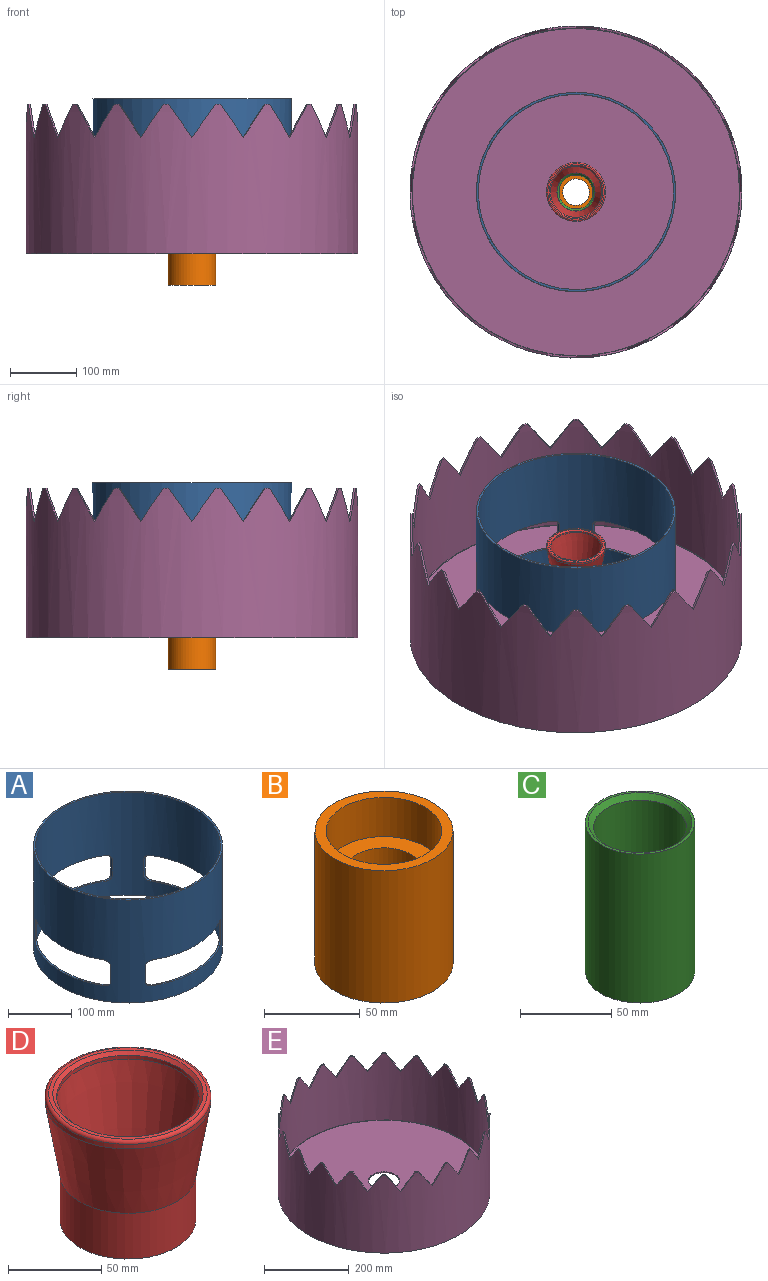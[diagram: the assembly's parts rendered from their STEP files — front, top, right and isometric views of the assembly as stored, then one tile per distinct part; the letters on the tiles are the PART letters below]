
ASSEMBLY  parts=5 mates=4
PART A: 36 faces, bbox 300x300x200 mm
  f0: plane 150x23.57mm, normal (0,0,-1), area 471.7mm2, adj f9,f15,f16,f17
  f1: cylinder r=10mm len=10mm, axis (1,0,0), area 56.4mm2, adj f2,f8,f16,f17
  f2: plane 30x3.66mm, normal (0,1,0), area 109.8mm2, adj f1,f3,f16,f17
  f3: cylinder r=10mm len=10mm, axis (1,0,0), area 56.4mm2, adj f2,f12,f16,f17
  f4: plane 150x23.57mm, normal (0,0,1), area 471.7mm2, adj f11,f13,f16,f17
  f5: cylinder r=10mm len=10mm, axis (1,0,0), area 56.4mm2, adj f6,f12,f16,f17
  f6: plane 30x3.66mm, normal (0,-1,0), area 109.8mm2, adj f5,f7,f16,f17
  f7: cylinder r=10mm len=10mm, axis (1,0,0), area 56.4mm2, adj f6,f8,f16,f17
  f8: plane 150x23.57mm, normal (0,0,-1), area 471.7mm2, adj f1,f7,f16,f17
  f9: cylinder r=10mm len=10mm, axis (1,0,0), area 56.4mm2, adj f0,f10,f16,f17
  f10: plane 30x3.66mm, normal (0,1,0), area 109.8mm2, adj f9,f11,f16,f17
  f11: cylinder r=10mm len=10mm, axis (1,0,0), area 56.4mm2, adj f4,f10,f16,f17
  f12: plane 150x23.57mm, normal (0,0,1), area 471.7mm2, adj f3,f5,f16,f17
  f13: cylinder r=10mm len=10mm, axis (1,0,0), area 56.4mm2, adj f4,f14,f16,f17
  f14: plane 30x3.66mm, normal (0,-1,0), area 109.8mm2, adj f13,f15,f16,f17
  f15: cylinder r=10mm len=10mm, axis (1,0,0), area 56.4mm2, adj f0,f14,f16,f17
  f16: cylinder r=147mm len=294mm, axis (0,0,-1), area 148887.5mm2, adj f0,f1,f2,f3,f4,f5,f6,f7
  f17: cylinder r=150mm len=300mm, axis (0,0,-1), area 152760mm2, adj f0,f1,f2,f3,f4,f5,f6,f7
  f18: plane 300x300mm, normal (0,0,1), area 2799.2mm2, adj f16,f17
  f19: plane 300x300mm, normal (0,0,-1), area 2799.2mm2, adj f16,f17
  f20: cylinder r=10mm len=10mm, axis (0,-1,0), area 56.4mm2, adj f16,f17,f21,f27
  f21: plane 30x3.66mm, normal (-1,0,0), area 109.8mm2, adj f16,f17,f20,f22
  f22: cylinder r=10mm len=10mm, axis (0,-1,0), area 56.4mm2, adj f16,f17,f21,f23
  f23: plane 150x23.57mm, normal (0,0,1), area 471.7mm2, adj f16,f17,f22,f24
  f24: cylinder r=10mm len=10mm, axis (0,-1,0), area 56.4mm2, adj f16,f17,f23,f25
  f25: plane 30x3.66mm, normal (1,0,0), area 109.8mm2, adj f16,f17,f24,f26
  f26: cylinder r=10mm len=10mm, axis (0,-1,0), area 56.4mm2, adj f16,f17,f25,f27
  f27: plane 150x23.57mm, normal (0,0,-1), area 471.7mm2, adj f16,f17,f20,f26
  f28: plane 150x23.57mm, normal (0,0,-1), area 471.7mm2, adj f16,f17,f29,f35
  f29: cylinder r=10mm len=10mm, axis (0,-1,0), area 56.4mm2, adj f16,f17,f28,f30
  f30: plane 30x3.66mm, normal (1,0,0), area 109.8mm2, adj f16,f17,f29,f31
  f31: cylinder r=10mm len=10mm, axis (0,-1,0), area 56.4mm2, adj f16,f17,f30,f32
  f32: plane 150x23.57mm, normal (0,0,1), area 471.7mm2, adj f16,f17,f31,f33
  f33: cylinder r=10mm len=10mm, axis (0,-1,0), area 56.4mm2, adj f16,f17,f32,f34
  f34: plane 30x3.66mm, normal (-1,0,0), area 109.8mm2, adj f16,f17,f33,f35
  f35: cylinder r=10mm len=10mm, axis (0,-1,0), area 56.4mm2, adj f16,f17,f28,f34
PART B: 8 faces, bbox 72x72x84.5 mm
  f0: cylinder r=24.2mm len=48.4mm, axis (0,0,-1), area 3801.3mm2, adj f1,f7
  f1: plane 72x72mm, normal (0,0,-1), area 2231.7mm2, adj f0,f2
  f2: cylinder r=36mm len=84.5mm, axis (0,0,-1), area 19113.4mm2, adj f1,f3
  f3: plane 72x72mm, normal (0,0,1), area 1206.2mm2, adj f2,f4
  f4: cylinder r=30.2mm len=60.4mm, axis (0,0,-1), area 4743.8mm2, adj f3,f5
  f5: plane 60.4x60.4mm, normal (0,0,1), area 1608.6mm2, adj f4,f6
  f6: cylinder r=20mm len=40mm, axis (0,0,-1), area 4335.4mm2, adj f5,f7
  f7: plane 48.4x48.4mm, normal (0,0,-1), area 583.2mm2, adj f0,f6
PART C: 6 faces, bbox 60x60x100 mm
  f0: cylinder r=25.5mm len=94mm, axis (0,0,-1), area 15060.8mm2, adj f4,f5
  f1: cylinder r=30mm len=100mm, axis (0,0,-1), area 18849.6mm2, adj f2,f3
  f2: plane 60x60mm, normal (0,0,1), area 275.7mm2, adj f1,f4
  f3: plane 60x60mm, normal (0,0,-1), area 275.7mm2, adj f1,f5
  f4: cone r=25.5mm half-angle=45deg, axis (0,0,1), area 719.7mm2, adj f0,f2
  f5: cone r=28.5mm half-angle=45deg, axis (0,0,-1), area 719.7mm2, adj f0,f3
PART D: 11 faces, bbox 96.3x96.3x83 mm
  f0: plane 85x85mm, normal (0,0,1), area 572.3mm2, adj f9,f10
  f1: cylinder r=38.3mm len=76.6mm, axis (0,0,-1), area 596.9mm2, adj f2,f10
  f2: cone r=29.27mm half-angle=9.6deg, axis (0,0,1), area 11521.4mm2, adj f1,f3
  f3: plane 60.4x60.4mm, normal (0,0,-1), area 174mm2, adj f2,f4
  f4: cylinder r=30.2mm len=60.4mm, axis (0,0,-1), area 4743.8mm2, adj f3,f5
  f5: plane 72.8x72.8mm, normal (0,0,-1), area 1297.2mm2, adj f4,f6
  f6: cylinder r=36.4mm len=72.8mm, axis (0,0,-1), area 6861.2mm2, adj f5,f7
  f7: cone r=36.4mm half-angle=9.6deg, axis (0,0,1), area 12371.9mm2, adj f6,f8
  f8: cylinder r=44.5mm len=89mm, axis (0,0,-1), area 838.8mm2, adj f7,f9
  f9: torus R=42.5mm, axis (0,0,-1), area 864mm2, adj f0,f8
  f10: cone r=40.3mm half-angle=45deg, axis (0,0,1), area 698.4mm2, adj f0,f1
PART E: 69 faces, bbox 500x500x225 mm
  f0: cylinder r=247mm len=494mm, axis (0,0,-1), area 45782.4mm2, adj f61,f67
  f1: plane 8.19x4.18mm, normal (0,0,1), area 23.4mm2, adj f2,f58,f59,f63
  f2: plane 50x34.99mm, normal (0.78,-0.25,0.57), area 183.7mm2, adj f1,f3,f58,f59
  f3: plane 50x33.46mm, normal (-0.78,0.25,0.57), area 183.7mm2, adj f2,f4,f58,f59
  f4: plane 8.32x6.21mm, normal (0,0,1), area 23.4mm2, adj f3,f5,f58,f59
  f5: plane 50x31.55mm, normal (0.66,-0.48,0.57), area 183.7mm2, adj f4,f6,f58,f59
  f6: plane 50x28.64mm, normal (-0.66,0.48,0.57), area 183.7mm2, adj f5,f7,f58,f59
  f7: plane 7.64x7.64mm, normal (0,0,1), area 23.4mm2, adj f6,f8,f58,f59
  f8: plane 50x28.64mm, normal (0.48,-0.66,0.57), area 183.7mm2, adj f7,f9,f58,f59
  f9: plane 50x31.55mm, normal (-0.48,0.66,0.57), area 183.7mm2, adj f8,f10,f58,f59
  f10: plane 8.32x6.21mm, normal (0,0,1), area 23.4mm2, adj f9,f11,f58,f59
  f11: plane 50x33.46mm, normal (0.25,-0.78,0.57), area 183.7mm2, adj f10,f12,f58,f59
  f12: plane 50x34.99mm, normal (-0.25,0.78,0.57), area 183.7mm2, adj f11,f13,f58,f59
  f13: plane 8.19x4.18mm, normal (0,0,1), area 23.4mm2, adj f12,f14,f58,f59
  f14: plane 50x35.01mm, normal (0,-0.82,0.57), area 183.7mm2, adj f13,f15,f58,f59
  f15: plane 50x35.01mm, normal (0,0.82,0.57), area 183.7mm2, adj f14,f16,f58,f59
  f16: plane 8.19x4.18mm, normal (0,0,1), area 23.4mm2, adj f15,f17,f58,f59
  f17: plane 50x34.99mm, normal (-0.25,-0.78,0.57), area 183.7mm2, adj f16,f18,f58,f59
  f18: plane 50x33.46mm, normal (0.25,0.78,0.57), area 183.7mm2, adj f17,f19,f58,f59
  f19: plane 8.32x6.21mm, normal (0,0,1), area 23.4mm2, adj f18,f20,f58,f59
  f20: plane 50x31.55mm, normal (-0.48,-0.66,0.57), area 183.7mm2, adj f19,f21,f58,f59
  f21: plane 50x28.64mm, normal (0.48,0.66,0.57), area 183.7mm2, adj f20,f22,f58,f59
  f22: plane 7.64x7.64mm, normal (0,0,1), area 23.4mm2, adj f21,f23,f58,f59
  f23: plane 50x28.64mm, normal (-0.66,-0.48,0.57), area 183.7mm2, adj f22,f24,f58,f59
  f24: plane 50x31.55mm, normal (0.66,0.48,0.57), area 183.7mm2, adj f23,f25,f58,f59
  f25: plane 8.32x6.21mm, normal (0,0,1), area 23.4mm2, adj f24,f26,f58,f59
  f26: plane 50x33.46mm, normal (-0.78,-0.25,0.57), area 183.7mm2, adj f25,f27,f58,f59
  f27: plane 50x34.99mm, normal (0.78,0.25,0.57), area 183.7mm2, adj f26,f28,f58,f59
  f28: plane 8.19x4.18mm, normal (0,0,1), area 23.4mm2, adj f27,f29,f58,f59
  f29: plane 50x35.01mm, normal (-0.82,0,0.57), area 183.7mm2, adj f28,f30,f58,f59
  f30: plane 50x35.01mm, normal (0.82,0,0.57), area 183.7mm2, adj f29,f31,f58,f59
  f31: plane 8.19x4.18mm, normal (0,0,1), area 23.4mm2, adj f30,f32,f58,f59
  f32: plane 50x34.99mm, normal (-0.78,0.25,0.57), area 183.7mm2, adj f31,f33,f58,f59
  f33: plane 50x33.46mm, normal (0.78,-0.25,0.57), area 183.7mm2, adj f32,f34,f58,f59
  f34: plane 8.32x6.21mm, normal (0,0,1), area 23.4mm2, adj f33,f35,f58,f59
  f35: plane 50x31.55mm, normal (-0.66,0.48,0.57), area 183.7mm2, adj f34,f36,f58,f59
  f36: plane 50x28.64mm, normal (0.66,-0.48,0.57), area 183.7mm2, adj f35,f37,f58,f59
  f37: plane 7.64x7.64mm, normal (0,0,1), area 23.4mm2, adj f36,f38,f58,f59
  f38: plane 50x28.64mm, normal (-0.48,0.66,0.57), area 183.7mm2, adj f37,f39,f58,f59
  f39: plane 50x31.55mm, normal (0.48,-0.66,0.57), area 183.7mm2, adj f38,f40,f58,f59
  f40: plane 8.32x6.21mm, normal (0,0,1), area 23.4mm2, adj f39,f41,f58,f59
  f41: plane 50x33.46mm, normal (-0.25,0.78,0.57), area 183.7mm2, adj f40,f42,f58,f59
  f42: plane 50x34.99mm, normal (0.25,-0.78,0.57), area 183.7mm2, adj f41,f43,f58,f59
  f43: plane 8.19x4.18mm, normal (0,0,1), area 23.4mm2, adj f42,f44,f58,f59
  f44: plane 50x35.01mm, normal (0,0.82,0.57), area 183.7mm2, adj f43,f45,f58,f59
  f45: plane 50x35.01mm, normal (0,-0.82,0.57), area 183.7mm2, adj f44,f46,f58,f59
  f46: plane 8.19x4.18mm, normal (0,0,1), area 23.4mm2, adj f45,f47,f58,f59
  f47: plane 50x34.99mm, normal (0.25,0.78,0.57), area 183.7mm2, adj f46,f48,f58,f59
  f48: plane 50x33.46mm, normal (-0.25,-0.78,0.57), area 183.7mm2, adj f47,f49,f58,f59
  f49: plane 8.32x6.21mm, normal (0,0,1), area 23.4mm2, adj f48,f50,f58,f59
  f50: plane 50x31.55mm, normal (0.48,0.66,0.57), area 183.7mm2, adj f49,f51,f58,f59
  f51: plane 50x28.64mm, normal (-0.48,-0.66,0.57), area 183.7mm2, adj f50,f52,f58,f59
  f52: plane 7.64x7.64mm, normal (0,0,1), area 23.4mm2, adj f51,f53,f58,f59
  f53: plane 50x28.64mm, normal (0.66,0.48,0.57), area 183.7mm2, adj f52,f54,f58,f59
  f54: plane 50x31.55mm, normal (-0.66,-0.48,0.57), area 183.7mm2, adj f53,f55,f58,f59
  f55: plane 8.32x6.21mm, normal (0,0,1), area 23.4mm2, adj f54,f56,f58,f59
  f56: plane 50x33.46mm, normal (0.78,0.25,0.57), area 183.7mm2, adj f55,f57,f58,f59
  f57: plane 50x34.99mm, normal (-0.78,-0.25,0.57), area 183.7mm2, adj f56,f58,f59,f60
  f58: cylinder r=247mm len=494mm, axis (0,0,-1), area 262128.5mm2, adj f1,f2,f3,f4,f5,f6,f7,f8
  f59: cylinder r=250mm len=500mm, axis (0,0,-1), area 318361.2mm2, adj f1,f2,f3,f4,f5,f6,f7,f8
  f60: plane 8.19x4.18mm, normal (0,0,1), area 23.4mm2, adj f57,f58,f59,f62
  f61: plane 500x500mm, normal (0,0,-1), area 4684.1mm2, adj f0,f59
  f62: plane 50x35.01mm, normal (0.82,0,0.57), area 183.7mm2, adj f58,f59,f60,f63
  f63: plane 50x35.01mm, normal (-0.82,0,0.57), area 183.7mm2, adj f1,f58,f59,f62
  f64: plane 493x493mm, normal (0,0,-1), area 186818.7mm2, adj f67,f68
  f65: plane 493x493mm, normal (0,0,1), area 186818.7mm2, adj f66,f68
  f66: cone r=246.5mm half-angle=45deg, axis (0,0,1), area 1096.3mm2, adj f58,f65
  f67: cone r=247mm half-angle=45deg, axis (0,0,-1), area 1096.3mm2, adj f0,f64
  f68: cylinder r=36mm len=72mm, axis (0,0,-1), area 678.6mm2, adj f64,f65
PLACE A t=(-59.72,31.1,18.86)mm
PLACE B t=(-59.72,31.1,-61.64)mm
PLACE C t=(-59.72,31.1,-2.14)mm
PLACE D t=(-59.72,31.1,72.86)mm
PLACE E t=(-59.72,31.1,-14.14)mm
MATE fastened A.f16 <-> E.f0  axis (0,0,-1) through (-59.72,31.1,18.86)mm
MATE fastened B.f0 <-> C.f0  axis (0,0,1) through (-59.72,31.1,-2.14)mm
MATE fastened C.f1 <-> D.f1  axis (0,0,1) through (-59.72,31.1,97.86)mm
MATE fastened D.f1 <-> E.f0  axis (0,0,1) through (-59.72,31.1,155.86)mm
